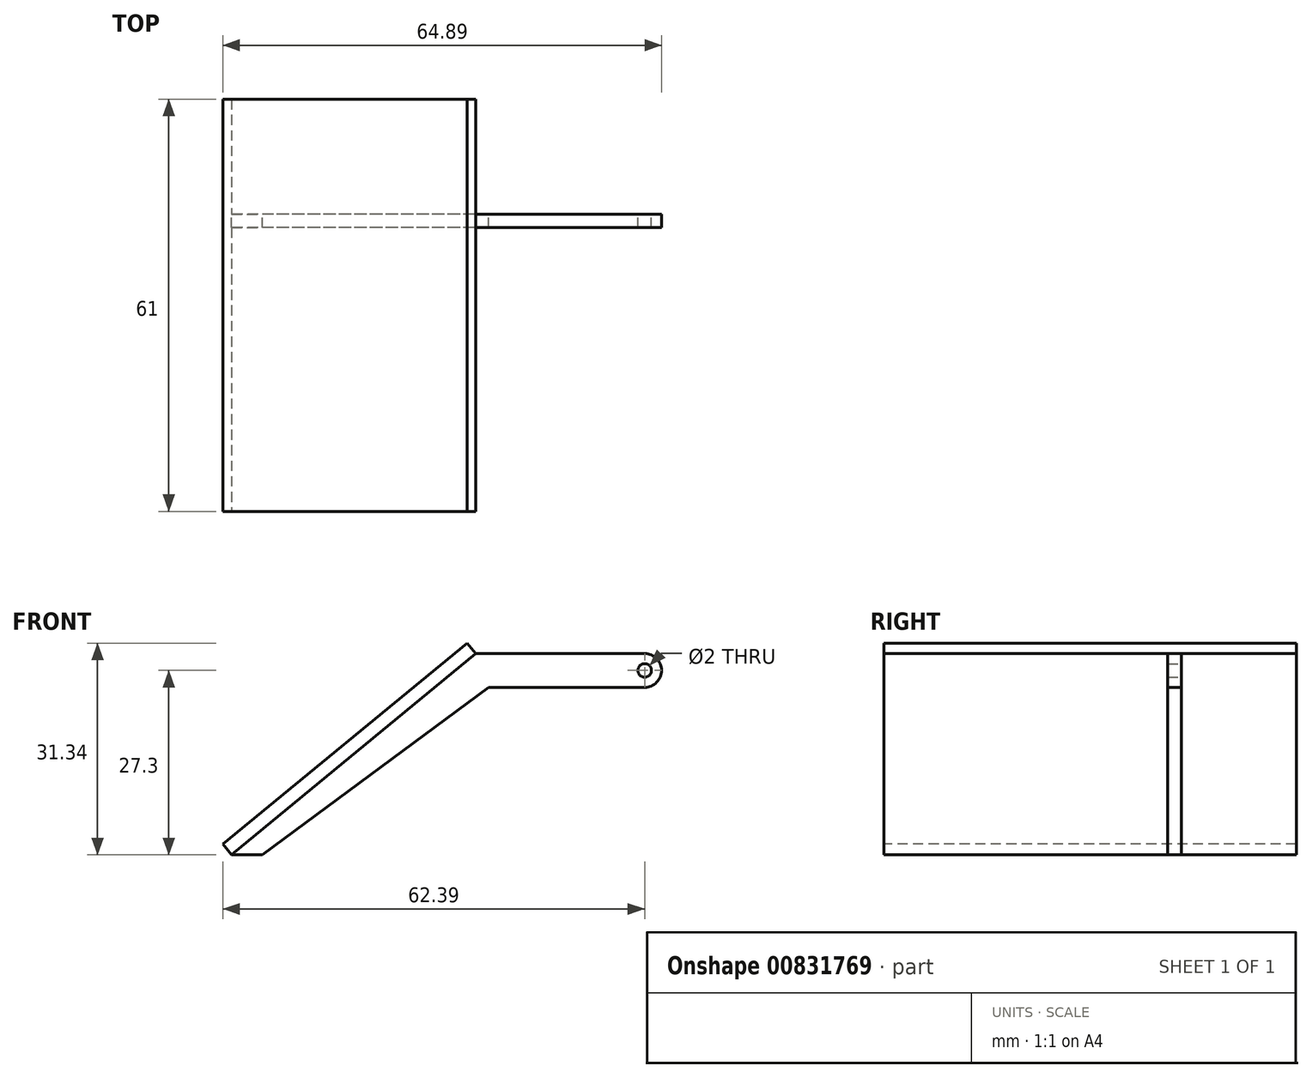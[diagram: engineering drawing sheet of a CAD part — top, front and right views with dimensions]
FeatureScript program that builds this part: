
annotation { "Feature Type Name" : "Feature", "Feature Type Description" : "" }
export const myFeature = defineFeature(function(context is Context, id is Id, definition is map)
    precondition{}
    {
        {
            var Q0;
            Q0=qCreatedBy(makeId("Front.planeOp"),FACE);
            var sketch = newSketch(context, id + "F0", { "sketchPlane" : qUnion([Q0])});
            skCircle(sketch, "E0", {"center": v(0, 0) * mm, "radius": 1 * mm});
            skCircle(sketch, "E1", {"center": v(0, 0) * mm, "radius": 2.5 * mm});
            skLineSegment(sketch, "E2", {"start": v(0, 2.5) * mm, "end": v(-25, 2.5) * mm});
            skLineSegment(sketch, "E3", {"start": v(-25, 2.5) * mm, "end": v(-61.12, -27.26) * mm});
            skLineSegment(sketch, "E4", {"start": v(0, -2.5) * mm, "end": v(-23.06, -2.5) * mm});
            skLineSegment(sketch, "E5", {"start": v(-23.06, -2.5) * mm, "end": v(-56.57, -27.3) * mm});
            skLineSegment(sketch, "E6", {"start": v(-61.12, -27.26) * mm, "end": v(-56.57, -27.3) * mm});
            skSolve(sketch);
        }
        {
            var Q0;
            {var subQ1=sQuery(id+"F0.wireOp",EDGE,"E2");Q0=makeQuery(id+"F0.imprint","IMPRINT",FACE,{"disambiguationData":[TD([[makeQuery(id+"F0.imprint","IMPRINT",EDGE,{"derivedFrom":subQ1}),1.0]])]});}
            var Q1;
            Q1=makeQuery(id+"F0.imprint","IMPRINT",FACE,{"disambiguationData":[TD([[makeQuery(id+"F0.imprint","IMPRINT",EDGE,{"derivedFrom":sQuery(id+"F0.wireOp",EDGE,"E0")}),-1.0]])]});
            extrude(context, id + "F1", {"entities" : qUnion([Q0, Q1]), "depth" : 2 * mm, "offsetDistance" : 25 * mm});
        }
        {
            var Q0;
            Q0=makeQuery(id+"F1.opExtrude","SWEPT_FACE",FACE,{"disambiguationData":[OSD([sQuery(id+"F0.wireOp",EDGE,"E3")])]});
            var sketch = newSketch(context, id + "F2", { "sketchPlane" : qUnion([Q0])});
            skLineSegment(sketch, "E7.bottom", {"start": v(-64.5, 17) * mm, "end": v(-17.7, 17) * mm});
            skLineSegment(sketch, "E7.top", {"start": v(-64.5, -44) * mm, "end": v(-17.7, -44) * mm});
            skLineSegment(sketch, "E7.left", {"start": v(-64.5, 17) * mm, "end": v(-64.5, -44) * mm});
            skLineSegment(sketch, "E7.right", {"start": v(-17.7, 17) * mm, "end": v(-17.7, -44) * mm});
            skSolve(sketch);
        }
        {
            var Q0;
            {var subQ0=sQuery(id+"F2.wireOp",EDGE,"E7.bottom");Q0=makeQuery(id+"F2.imprint","IMPRINT",FACE,{"disambiguationData":[TD([[makeQuery(id+"F2.imprint","IMPRINT",EDGE,{"derivedFrom":subQ0}),-1.0]])]});}
            var Q1;
            {var subQ1=sQuery(id+"F0.wireOp",EDGE,"E3");var subQ2=makeQuery(id+"F1.opExtrude","CAP_EDGE",EDGE,{"disambiguationData":[OSD([subQ1])],"isStart":true});Q1=makeQuery(id+"F2.imprint","IMPRINT",FACE,{"disambiguationData":[TD([[makeQuery(id+"F2.imprint","IMPRINT",EDGE,{"derivedFrom":subQ2}),1.0]])]});}
            var Q2;
            {var subQ0=sQuery(id+"F2.wireOp",EDGE,"E7.top");Q2=makeQuery(id+"F2.imprint","IMPRINT",FACE,{"disambiguationData":[TD([[makeQuery(id+"F2.imprint","IMPRINT",EDGE,{"derivedFrom":subQ0}),1.0]])]});}
            extrude(context, id + "F3", {"entities" : qUnion([Q0, Q1, Q2]), "operationType" : NewBodyOperationType.ADD, "depth" : 2 * mm, "offsetDistance" : 25 * mm});
        }
    });
